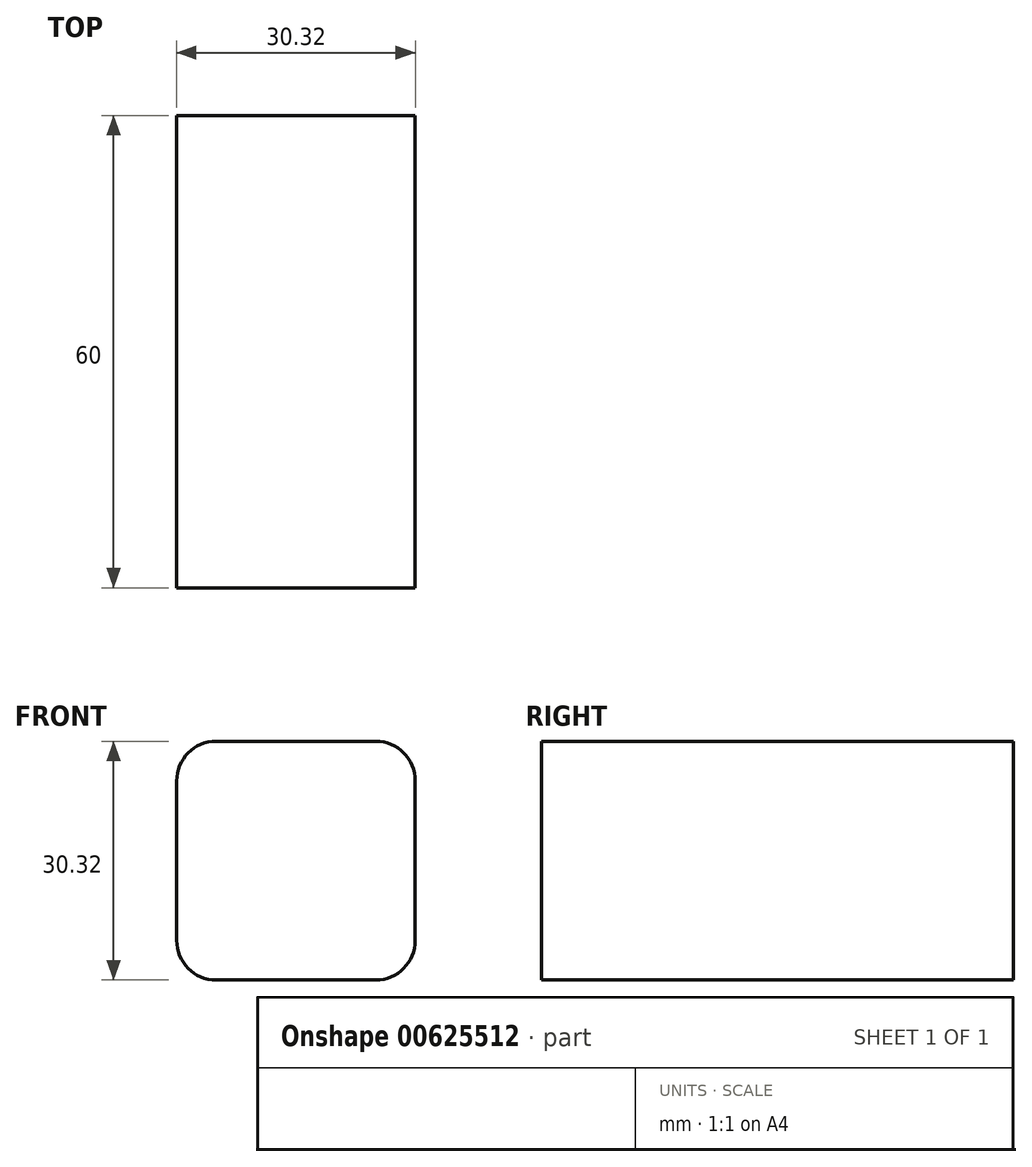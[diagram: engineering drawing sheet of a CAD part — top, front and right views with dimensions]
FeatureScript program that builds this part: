
annotation { "Feature Type Name" : "Feature", "Feature Type Description" : "" }
export const myFeature = defineFeature(function(context is Context, id is Id, definition is map)
    precondition{}
    {
        {
            var Q0;
            Q0=qCreatedBy(makeId("Front.planeOp"),FACE);
            var sketch = newSketch(context, id + "F0", { "sketchPlane" : qUnion([Q0])});
            skLineSegment(sketch, "E0.bottom", {"start": v(15.16, -15.16) * mm, "end": v(-15.16, -15.16) * mm});
            skLineSegment(sketch, "E0.top", {"start": v(15.16, 15.16) * mm, "end": v(-15.16, 15.16) * mm});
            skLineSegment(sketch, "E0.left", {"start": v(15.16, -15.16) * mm, "end": v(15.16, 15.16) * mm});
            skLineSegment(sketch, "E0.right", {"start": v(-15.16, -15.16) * mm, "end": v(-15.16, 15.16) * mm});
            skPoint(sketch, "E0.middle", {"position": v(0, 0) * mm});
            skSolve(sketch);
        }
        {
            var Q0;
            Q0 = qSketchRegion(id + "F0", true);
            extrude(context, id + "F1", {"entities" : qUnion([Q0]), "depth" : 60 * mm, "offsetDistance" : 25 * mm});
        }
        {
            var Q0;
            Q0=makeQuery(id+"F1.opExtrude","SWEPT_EDGE",EDGE,{"disambiguationData":[OSD([sQuery(id+"F0.wireOp",EDGE,"E0.top"),sQuery(id+"F0.wireOp",EDGE,"E0.right")])]});
            var Q1;
            Q1=makeQuery(id+"F1.opExtrude","SWEPT_EDGE",EDGE,{"disambiguationData":[OSD([sQuery(id+"F0.wireOp",EDGE,"E0.top"),sQuery(id+"F0.wireOp",EDGE,"E0.left")])]});
            var Q2;
            Q2=makeQuery(id+"F1.opExtrude","SWEPT_EDGE",EDGE,{"disambiguationData":[OSD([sQuery(id+"F0.wireOp",EDGE,"E0.bottom"),sQuery(id+"F0.wireOp",EDGE,"E0.right")])]});
            var Q3;
            Q3=makeQuery(id+"F1.opExtrude","SWEPT_EDGE",EDGE,{"disambiguationData":[OSD([sQuery(id+"F0.wireOp",EDGE,"E0.bottom"),sQuery(id+"F0.wireOp",EDGE,"E0.left")])]});
            fillet(context, id + "F2", {"entities" : qUnion([Q0, Q1, Q2, Q3]), "radius" : 5 * mm, "tangentPropagation" : true, "allowEdgeOverflow" : false});
        }
    });
